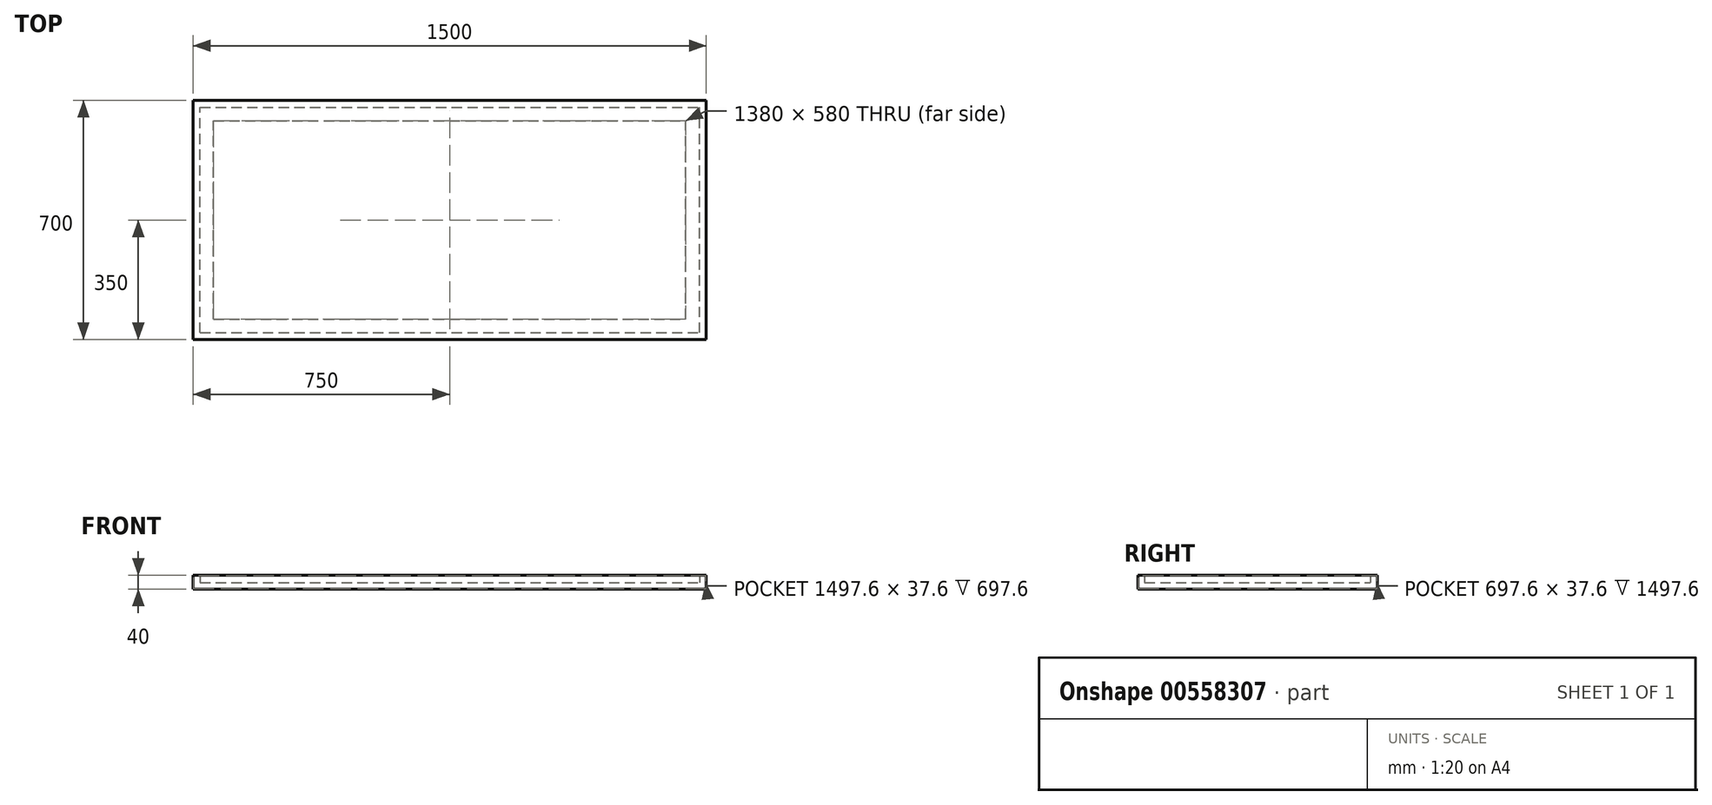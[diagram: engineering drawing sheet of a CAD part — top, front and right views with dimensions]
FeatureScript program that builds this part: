
annotation { "Feature Type Name" : "Feature", "Feature Type Description" : "" }
export const myFeature = defineFeature(function(context is Context, id is Id, definition is map)
    precondition{}
    {
        {
            assignVariable(context, id + "F0", {"name" : "Spessore_Piano", "anyValue" : 1.2});
        }
        {
            var Q0;
            Q0=qCreatedBy(makeId("Top.planeOp"),FACE);
            var sketch = newSketch(context, id + "F1", { "sketchPlane" : qUnion([Q0])});
            skLineSegment(sketch, "E0.bottom", {"start": v(0, 0) * mm, "end": v(1500, 0) * mm});
            skLineSegment(sketch, "E0.top", {"start": v(0, 700) * mm, "end": v(1500, 700) * mm});
            skLineSegment(sketch, "E0.left", {"start": v(0, 0) * mm, "end": v(0, 700) * mm});
            skLineSegment(sketch, "E0.right", {"start": v(1500, 0) * mm, "end": v(1500, 700) * mm});
            skLineSegment(sketch, "E1.0", {"start": v(60, 60) * mm, "end": v(60, 640) * mm});
            skLineSegment(sketch, "E1.1", {"start": v(60, 60) * mm, "end": v(1440, 60) * mm});
            skLineSegment(sketch, "E1.2", {"start": v(1440, 60) * mm, "end": v(1440, 640) * mm});
            skLineSegment(sketch, "E1.3", {"start": v(60, 640) * mm, "end": v(1440, 640) * mm});
            skLineSegment(sketch, "E2", {"start": v(0, 350) * mm, "end": v(1500, 350) * mm, "construction": true});
            skLineSegment(sketch, "E3", {"start": v(750, 0) * mm, "end": v(750, 700) * mm, "construction": true});
            skSolve(sketch);
        }
        {
            var Q0;
            Q0=qSketchRegion(id+"F1",true);
            var Q1;
            Q1=makeQuery(id+"F1.imprint","IMPRINT",FACE,{"disambiguationData":[TD([[makeQuery(id+"F1.imprint","IMPRINT",EDGE,{"derivedFrom":sQuery(id+"F1.wireOp",EDGE,"E1.0")}),-1.0]])]});
            extrude(context, id + "F2", {"entities" : qUnion([Q0, Q1]), "depth" : 40 * mm});
        }
        {
            var Q0;
            Q0=makeQuery(id+"F2.opExtrude","CAP_FACE",FACE,{"disambiguationData":[OSD([sQuery(id+"F1.wireOp",EDGE,"E0.bottom"),sQuery(id+"F1.wireOp",EDGE,"E0.top"),sQuery(id+"F1.wireOp",EDGE,"E0.left"),sQuery(id+"F1.wireOp",EDGE,"E0.right")])],"isStart":true});
            shell(context, id + "F3", {"entities" : qUnion([Q0]), "thickness" : (getVariable(context, 'Spessore_Piano')) * mm});
        }
        {
            var Q0;
            Q0=makeQuery(id+"F1.imprint","IMPRINT",FACE,{"disambiguationData":[TD([[makeQuery(id+"F1.imprint","IMPRINT",EDGE,{"derivedFrom":sQuery(id+"F1.wireOp",EDGE,"E0.bottom")}),1.0]])]});
            extrude(context, id + "F4", {"entities" : qUnion([Q0]), "operationType" : NewBodyOperationType.ADD, "depth" : (getVariable(context, 'Spessore_Piano')) * mm, "offsetDistance" : 25 * mm});
        }
        {
            var Q0;
            Q0=qCreatedBy(makeId("Top.planeOp"),FACE);
            var sketch = newSketch(context, id + "F5", { "sketchPlane" : qUnion([Q0])});
            skLineSegment(sketch, "E4.bottom", {"start": v(20, 20) * mm, "end": v(1480, 20) * mm});
            skLineSegment(sketch, "E4.top", {"start": v(20, 680) * mm, "end": v(1480, 680) * mm});
            skLineSegment(sketch, "E4.left", {"start": v(20, 20) * mm, "end": v(20, 680) * mm});
            skLineSegment(sketch, "E4.right", {"start": v(1480, 20) * mm, "end": v(1480, 680) * mm});
            skLineSegment(sketch, "E5", {"start": v(750, 680) * mm, "end": v(750, 20) * mm, "construction": true});
            skLineSegment(sketch, "E6", {"start": v(1480, 350) * mm, "end": v(20, 350) * mm, "construction": true});
            skPoint(sketch, "E7", {"position": v(750, 350) * mm});
            skSolve(sketch);
        }
        {
            var Q0;
            Q0=qSketchRegion(id+"F5",true);
            extrude(context, id + "F6", {"entities" : qUnion([Q0]), "depth" : (40 - getVariable(context, 'Spessore_Piano')) * mm, "hasSecondDirection" : true, "secondDirectionOppositeDirection" : true, "secondDirectionDepth" : (-20 + getVariable(context, 'Spessore_Piano')) * mm, "offsetDistance" : 25 * mm});
        }
    });
